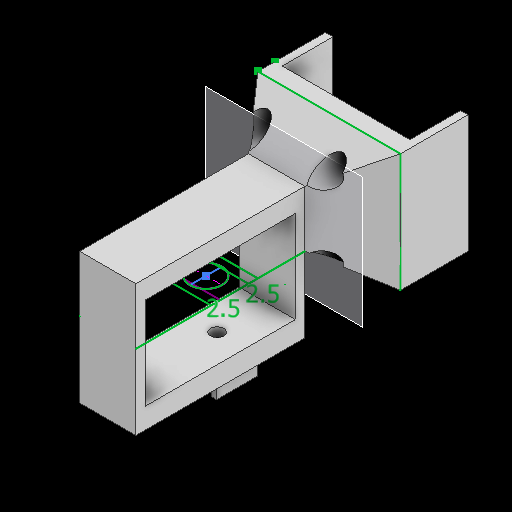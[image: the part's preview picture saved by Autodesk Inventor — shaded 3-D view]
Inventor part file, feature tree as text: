
AUTODESK INVENTOR PART (.ipt)
format: ipt  version: 2025.1 (Build 291241000, 241)  size: 340,480 bytes
history: native  units: in
note: dims shown in document units (in); Inventor stores cm internally (conversion verified against a paired STEP export)
features: sketch x29, extrude x19, projected_geometry x12, other x6, loft x1
ambient origin geometry x8: Origin, YZ Plane, XZ Plane, XY Plane, X Axis, Y Axis, Z Axis, Center Point
bodies: Body1 (feature_tree)
feature tree (67):
  other  "솔리드1"
  extrude  "돌출1"  Depth=1.4961in
  extrude  "돌출2"  Depth=1.2402in
  sketch  "스케치3"
  other  "작업 평면1"
  sketch  "스케치4"
  loft  "로프트1"
  extrude  "돌출3"  Depth=0.0787in
  sketch  "스케치7"
  other  "작업 평면2"
  sketch  "스케치8"
  sketch  "스케치9"
  sketch  "스케치10"
  extrude  "돌출4"  Depth=0.0787in
  extrude  "돌출5"  Depth=0.5315in TaperAngle=0.0deg
  extrude  "돌출6"  Depth=0.4724in
  extrude  "돌출7"  Depth=0.6693in
  extrude  "돌출8"  Depth=0.6201in
  sketch  "스케치14"
  sketch  "스케치15"
  extrude  "돌출10"  Depth=0.5906in
  sketch  "스케치17"
  sketch  "스케치18"
  sketch  "스케치19"
  extrude  "돌출11"  Depth=0.5906in
  extrude  "돌출12"  Depth=0.2953in
  extrude  "돌출13"  Depth=0.2953in
  sketch  "스케치22"
  extrude  "돌출14"  TaperAngle=0.0deg  [1 undecoded]
  extrude  "돌출15"  TaperAngle=0.0deg  [1 undecoded]
  extrude  "돌출16"  Depth=0.1575in
  extrude  "돌출17"  Depth=0.1969in
  sketch  "스케치27"
  extrude  "돌출18"  Depth=0.2165in
  extrude  "돌출19"  Depth=0.7874in
  extrude  "돌출20"  Depth=0.7874in
  sketch  "스케치1"
  sketch  "스케치2"
  projected_geometry  "투영된 루프1"
  projected_geometry  "투영된 루프2"
  sketch  "스케치5"
  other  "모서리1"
  sketch  "스케치6"
  projected_geometry  "투영된 루프3"
  other  "스케치 - 직사각형 패턴1"
  other  "스케치 - 직사각형 패턴2"
  sketch  "스케치11"
  sketch  "스케치12"
  projected_geometry  "투영된 루프4"
  projected_geometry  "투영된 루프5"
  projected_geometry  "투영된 루프6"
  sketch  "스케치16"
  projected_geometry  "투영된 루프7"
  projected_geometry  "투영된 루프8"
  sketch  "스케치20"
  sketch  "스케치21"
  projected_geometry  "투영된 루프9"
  sketch  "스케치23"
  sketch  "스케치24"
  sketch  "스케치25"
  projected_geometry  "투영된 루프10"
  sketch  "스케치26"
  projected_geometry  "투영된 루프11"
  projected_geometry  "투영된 루프12"
  sketch  "스케치28"
  sketch  "스케치29"
  sketch  "스케치30"
note: 2 required parameter values undecoded (feature->parameter linkage not recoverable at this tier; creation-order binding heuristic only, values carry confidence <= 0.55)
